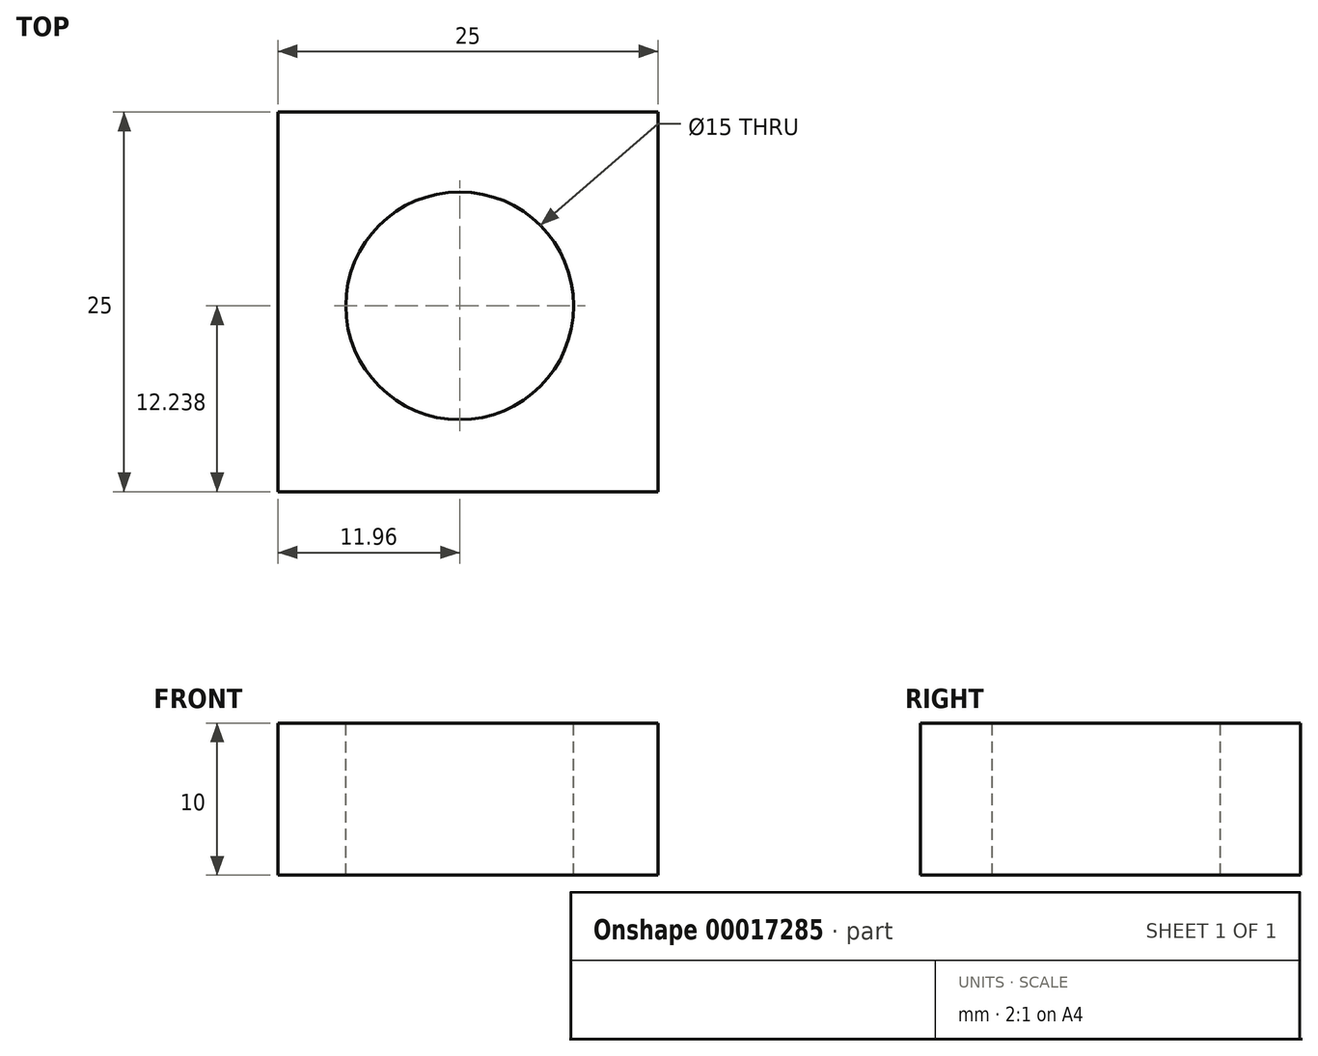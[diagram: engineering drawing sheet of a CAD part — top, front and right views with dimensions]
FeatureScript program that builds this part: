
annotation { "Feature Type Name" : "Feature", "Feature Type Description" : "" }
export const myFeature = defineFeature(function(context is Context, id is Id, definition is map)
    precondition{}
    {
        {
            var Q0;
            Q0=qCreatedBy(makeId("Front.planeOp"),FACE);
            var sketch = newSketch(context, id + "F0", { "sketchPlane" : qUnion([Q0])});
            skLineSegment(sketch, "E0.bottom", {"start": v(-25, 0) * mm, "end": v(0, 0) * mm});
            skLineSegment(sketch, "E0.top", {"start": v(-25, -10) * mm, "end": v(0, -10) * mm});
            skLineSegment(sketch, "E0.left", {"start": v(-25, 0) * mm, "end": v(-25, -10) * mm});
            skLineSegment(sketch, "E0.right", {"start": v(0, 0) * mm, "end": v(0, -10) * mm});
            skSolve(sketch);
        }
        {
            var Q0;
            Q0=makeQuery(id+"F0.imprint","IMPRINT",FACE,{"disambiguationData":[TD([[makeQuery(id+"F0.imprint","IMPRINT",EDGE,{"derivedFrom":sQuery(id+"F0.wireOp",EDGE,"E0.bottom")}),-1.0]])]});
            extrude(context, id + "F1", {"entities" : qUnion([Q0]), "depth" : 25 * mm});
        }
        {
            var Q0;
            Q0=makeQuery(id+"F1.opExtrude","SWEPT_FACE",FACE,{"disambiguationData":[OSD([sQuery(id+"F0.wireOp",EDGE,"E0.bottom")])]});
            var sketch = newSketch(context, id + "F2", { "sketchPlane" : qUnion([Q0])});
            skCircle(sketch, "E1", {"center": v(-13.04, -12.76) * mm, "radius": 7.5 * mm});
            skPoint(sketch, "E2", {"position": v(-20.53, -13.09) * mm});
            skPoint(sketch, "E3", {"position": v(-5.55, -13.09) * mm});
            skPoint(sketch, "E4", {"position": v(-13.36, -5.27) * mm});
            skPoint(sketch, "E5", {"position": v(-12.99, -20.26) * mm});
            skSolve(sketch);
        }
        {
            var Q0;
            Q0=sQuery(id+"F2.wireOp",VERTEX,"E1.center");
            var Q1;
            Q1=makeQuery(id+"F1.opExtrude","SWEPT_BODY",BODY,{"disambiguationData":[OSD([sQuery(id+"F0.wireOp",EDGE,"E0.bottom"),sQuery(id+"F0.wireOp",EDGE,"E0.top"),sQuery(id+"F0.wireOp",EDGE,"E0.left"),sQuery(id+"F0.wireOp",EDGE,"E0.right")])]});
            hole(context, id + "F3", {"style" : HoleStyle.SIMPLE, "holeDiameter" : 15 * mm, "endStyle" : HoleEndStyle.THROUGH, "locations" : qUnion([Q0]), "scope" : qUnion([Q1])});
        }
    });
